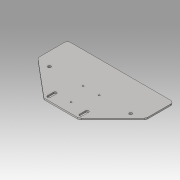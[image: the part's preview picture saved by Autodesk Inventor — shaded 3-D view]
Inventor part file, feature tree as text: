
AUTODESK INVENTOR PART (.ipt)
format: ipt  version: 2016 (Build 200138000, 138)  size: 207,360 bytes
history: native  units: in
note: dims shown in document units (in); Inventor stores cm internally (conversion verified against a paired STEP export)
features: sketch x8, extrude x4, hole x2
ambient origin geometry x8: Origin, YZ Plane, XZ Plane, XY Plane, X Axis, Y Axis, Z Axis, Center Point
bodies: Solid1 (feature_tree)
feature tree (14):
  extrude  "Extrusion1"  Depth=8.5in
  hole  "Hole1"  [1 undecoded]
  extrude  "Extrusion3"  Depth=3.1102in
  extrude  "Extrusion4"  Depth=0.25in
  extrude  "Extrusion5"  Depth=1.0236in
  sketch  "Sketch9"  dims[d24=0.2953in]
  hole  "Hole2"  [1 undecoded]
  sketch  "Sketch11"  dims[d40=3.8881in d43=1.0in d44=0.0in d45=1.75in d47=1.75in d48=1.75in d49=1.75in d50=2.382in d52=2.5591in d53=0.6398in d54=0.6398in d55=2.382in d58=2.0472in d62=1.2795in d64=0.1181in d65=0.75in d66=0.375in d67=0.25in d68=0.5635in d69=1.0in d70=0.8108in d72=0.2362in d76=0.236in d77=0.492in d78=0.236in d79=0.492in d80=1.0in d81=0.0in d82=0.236in d83=0.492in d84=0.236in d85=0.492in d86=1.0in d87=0.0in d88=0.2362in d93=0.2953in d95=2.3746in d96=2.07in d99=135.0deg d100=0.25in d101=0.25in d102=0.25in d103=0.25in d104=0.962in d125=0.0in d126=0.5445in d127=0.5445in d128=0.2722in d129=0.2722in]
  sketch  "Sketch1"  dims[d0=8.5in d1=6.0in]
  sketch  "Sketch2"  dims[d2=0.125in d3=0.0in d4=5.6831in]
  sketch  "Sketch3"  dims[d5=1.0236in d7=3.1102in]
  sketch  "Sketch5"  dims[d12=0.2362in d13=0.75in d14=0.375in d15=0.25in d16=0.5635in d17=1.0in d18=0.8108in d19=1.0768in]
  sketch  "Sketch7"  dims[d20=3.1102in d21=1.0236in]
  sketch  "Sketch8"  dims[d22=3.124in d23=7.5728in]
note: 2 required parameter values undecoded (feature->parameter linkage not recoverable at this tier; creation-order binding heuristic only, values carry confidence <= 0.55)
